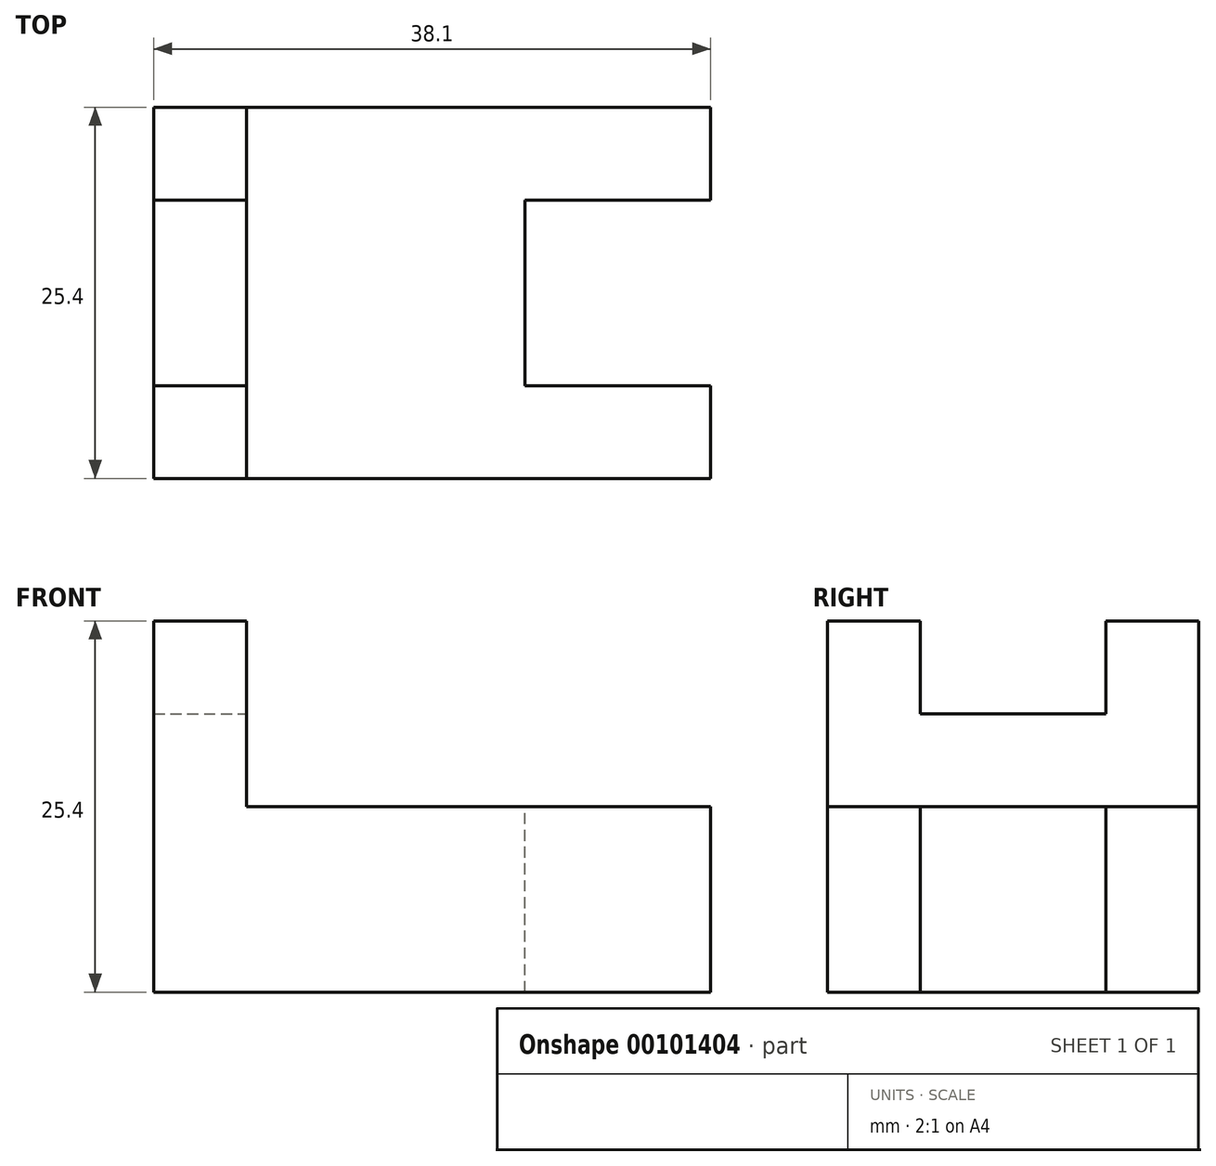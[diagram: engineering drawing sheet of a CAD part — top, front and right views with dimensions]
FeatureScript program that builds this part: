
annotation { "Feature Type Name" : "Feature", "Feature Type Description" : "" }
export const myFeature = defineFeature(function(context is Context, id is Id, definition is map)
    precondition{}
    {
        {
            var Q0;
            Q0=qCreatedBy(makeId("Front.planeOp"),FACE);
            var sketch = newSketch(context, id + "F0", { "sketchPlane" : qUnion([Q0])});
            skLineSegment(sketch, "E0", {"start": v(0, 0) * mm, "end": v(38.1, 0) * mm});
            skLineSegment(sketch, "E1", {"start": v(38.1, 0) * mm, "end": v(38.1, 12.7) * mm});
            skLineSegment(sketch, "E2", {"start": v(38.1, 12.7) * mm, "end": v(0, 12.7) * mm});
            skLineSegment(sketch, "E3", {"start": v(0, 12.7) * mm, "end": v(0, 0) * mm});
            skLineSegment(sketch, "E4", {"start": v(0, 12.7) * mm, "end": v(0, 25.4) * mm});
            skLineSegment(sketch, "E5", {"start": v(0, 25.4) * mm, "end": v(6.35, 25.4) * mm});
            skLineSegment(sketch, "E6", {"start": v(6.35, 25.4) * mm, "end": v(6.35, 12.7) * mm});
            skSolve(sketch);
        }
        {
            var Q0;
            Q0=makeQuery(id+"F0.imprint","IMPRINT",FACE,{"disambiguationData":[TD([[makeQuery(id+"F0.imprint","IMPRINT",EDGE,{"derivedFrom":sQuery(id+"F0.wireOp",EDGE,"E0")}),1.0]])]});
            extrude(context, id + "F1", {"entities" : qUnion([Q0]), "oppositeDirection" : true, "depth" : 25.4 * mm});
        }
        {
            var Q0;
            Q0=makeQuery(id+"F1.opExtrude","SWEPT_FACE",FACE,{"disambiguationData":[OSD([sQuery(id+"F0.wireOp",EDGE,"E1")])]});
            var sketch = newSketch(context, id + "F2", { "sketchPlane" : qUnion([Q0])});
            skLineSegment(sketch, "E7", {"start": v(6.35, 0) * mm, "end": v(6.35, 12.7) * mm});
            skLineSegment(sketch, "E8", {"start": v(6.35, 12.7) * mm, "end": v(19.05, 12.7) * mm});
            skLineSegment(sketch, "E9", {"start": v(19.05, 12.7) * mm, "end": v(19.05, 0) * mm});
            skLineSegment(sketch, "E10", {"start": v(19.05, 0) * mm, "end": v(6.35, 0) * mm});
            skSolve(sketch);
        }
        {
            var Q0;
            {var subQ0=sQuery(id+"F0.wireOp",EDGE,"E4");Q0=makeQuery(id+"F0.imprint","IMPRINT",FACE,{"disambiguationData":[TD([[makeQuery(id+"F0.imprint","IMPRINT",EDGE,{"derivedFrom":subQ0}),-1.0]])]});}
            extrude(context, id + "F3", {"entities" : qUnion([Q0]), "operationType" : NewBodyOperationType.ADD, "oppositeDirection" : true, "depth" : 25.4 * mm});
        }
        {
            var Q0;
            Q0=makeQuery(id+"F2.imprint","IMPRINT",FACE,{"disambiguationData":[TD([[makeQuery(id+"F2.imprint","IMPRINT",EDGE,{"derivedFrom":sQuery(id+"F2.wireOp",EDGE,"E7")}),-1.0]])]});
            extrude(context, id + "F4", {"entities" : qUnion([Q0]), "operationType" : NewBodyOperationType.REMOVE, "oppositeDirection" : true, "depth" : 12.7 * mm});
        }
        {
            var Q0;
            Q0=makeQuery(id+"F3.opExtrude","SWEPT_FACE",FACE,{"disambiguationData":[OSD([sQuery(id+"F0.wireOp",EDGE,"E6")])]});
            var sketch = newSketch(context, id + "F5", { "sketchPlane" : qUnion([Q0])});
            skLineSegment(sketch, "E11", {"start": v(6.35, 25.4) * mm, "end": v(6.35, 19.05) * mm});
            skLineSegment(sketch, "E12", {"start": v(6.35, 19.05) * mm, "end": v(19.05, 19.05) * mm});
            skLineSegment(sketch, "E13", {"start": v(19.05, 19.05) * mm, "end": v(19.05, 25.4) * mm});
            skLineSegment(sketch, "E14", {"start": v(19.05, 25.4) * mm, "end": v(6.35, 25.4) * mm});
            skSolve(sketch);
        }
        {
            var Q0;
            Q0=makeQuery(id+"F5.imprint","IMPRINT",FACE,{"disambiguationData":[TD([[makeQuery(id+"F5.imprint","IMPRINT",EDGE,{"derivedFrom":sQuery(id+"F5.wireOp",EDGE,"E11")}),1.0]])]});
            extrude(context, id + "F6", {"entities" : qUnion([Q0]), "operationType" : NewBodyOperationType.REMOVE, "oppositeDirection" : true, "depth" : 6.35 * mm});
        }
    });
